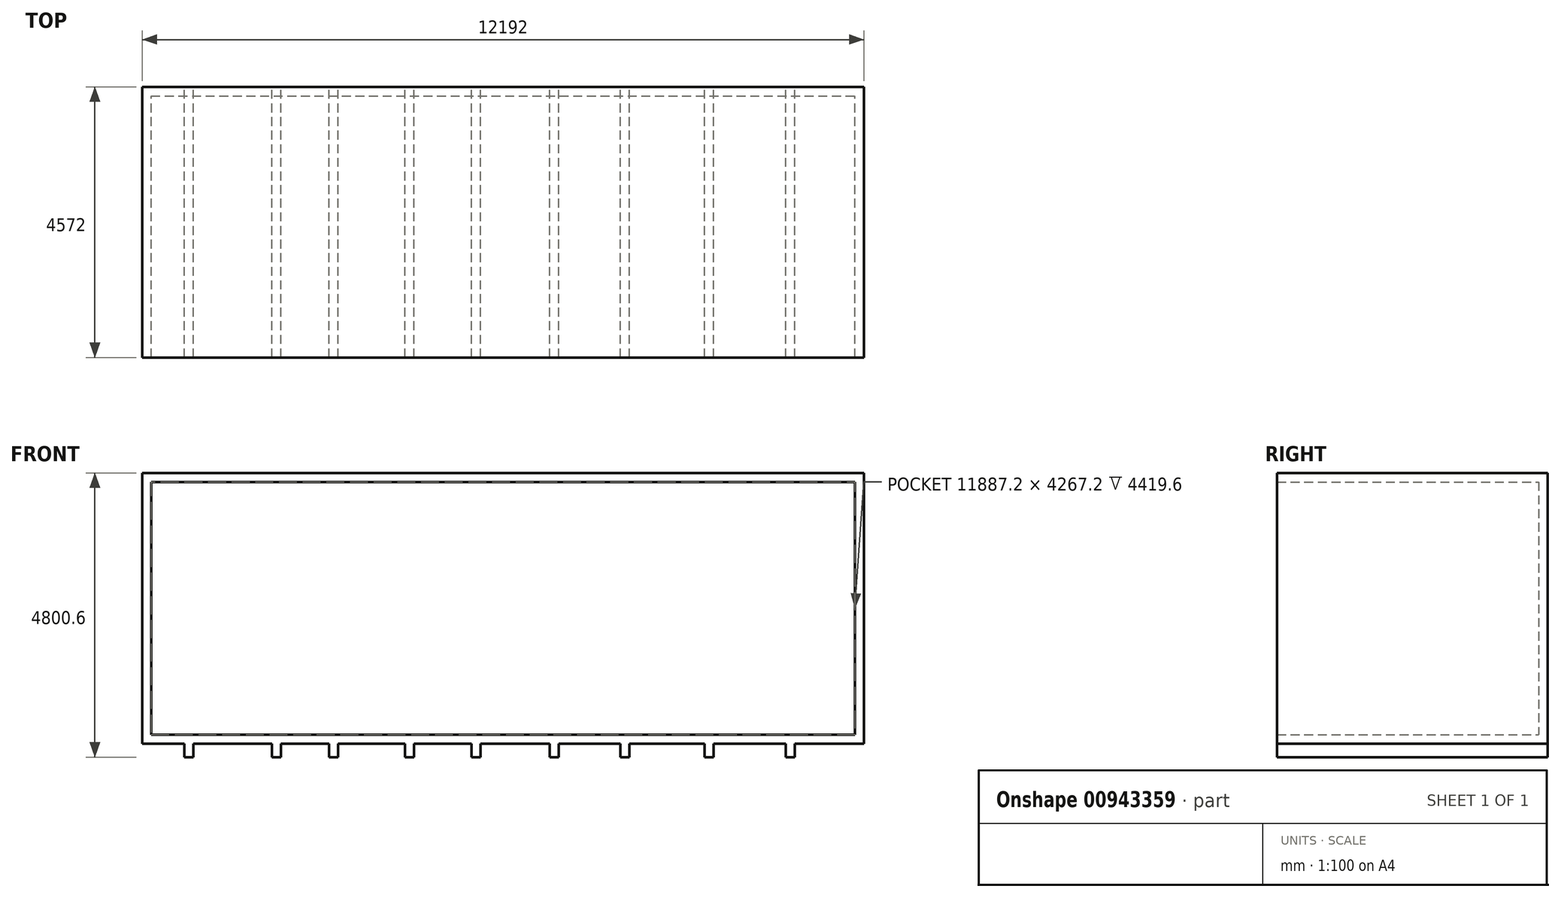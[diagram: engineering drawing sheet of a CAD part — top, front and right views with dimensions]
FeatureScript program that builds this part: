
annotation { "Feature Type Name" : "Feature", "Feature Type Description" : "" }
export const myFeature = defineFeature(function(context is Context, id is Id, definition is map)
    precondition{}
    {
        {
            var Q0;
            Q0=qCreatedBy(makeId("Front.planeOp"),FACE);
            var sketch = newSketch(context, id + "F0", { "sketchPlane" : qUnion([Q0])});
            skLineSegment(sketch, "E0.bottom", {"start": v(-6151.67, 2442.04) * mm, "end": v(6040.33, 2442.04) * mm});
            skLineSegment(sketch, "E0.top", {"start": v(-6151.67, -2129.96) * mm, "end": v(6040.33, -2129.96) * mm});
            skLineSegment(sketch, "E0.left", {"start": v(-6151.67, 2442.04) * mm, "end": v(-6151.67, -2129.96) * mm});
            skLineSegment(sketch, "E0.right", {"start": v(6040.33, 2442.04) * mm, "end": v(6040.33, -2129.96) * mm});
            skSolve(sketch);
        }
        {
            var Q0;
            Q0 = qSketchRegion(id + "F0", true);
            extrude(context, id + "F1", {"entities" : qUnion([Q0]), "depth" : 4572 * mm, "offsetDistance" : 25.4 * mm});
        }
        {
            var Q0;
            Q0=makeQuery(id+"F1.opExtrude","CAP_FACE",FACE,{"disambiguationData":[OSD([sQuery(id+"F0.wireOp",EDGE,"E0.bottom"),sQuery(id+"F0.wireOp",EDGE,"E0.top"),sQuery(id+"F0.wireOp",EDGE,"E0.left"),sQuery(id+"F0.wireOp",EDGE,"E0.right")])],"isStart":false});
            shell(context, id + "F2", {"entities" : qUnion([Q0]), "thickness" : 152.4 * mm});
        }
        {
            var Q0;
            Q0=makeQuery(id+"F1.opExtrude","SWEPT_FACE",FACE,{"disambiguationData":[OSD([sQuery(id+"F0.wireOp",EDGE,"E0.top")])]});
            var sketch = newSketch(context, id + "F3", { "sketchPlane" : qUnion([Q0])});
            skLineSegment(sketch, "E1.bottom", {"start": v(4875.4, 4572) * mm, "end": v(4723, 4572) * mm});
            skLineSegment(sketch, "E1.top", {"start": v(4875.4, 0) * mm, "end": v(4723, 0) * mm});
            skLineSegment(sketch, "E1.left", {"start": v(4875.4, 4572) * mm, "end": v(4875.4, 0) * mm});
            skLineSegment(sketch, "E1.right", {"start": v(4723, 4572) * mm, "end": v(4723, 0) * mm});
            skLineSegment(sketch, "E2.bottom", {"start": v(3502.69, 4572) * mm, "end": v(3350.29, 4572) * mm});
            skLineSegment(sketch, "E2.top", {"start": v(3502.69, 0) * mm, "end": v(3350.29, 0) * mm});
            skLineSegment(sketch, "E2.left", {"start": v(3502.69, 4572) * mm, "end": v(3502.69, 0) * mm});
            skLineSegment(sketch, "E2.right", {"start": v(3350.29, 4572) * mm, "end": v(3350.29, 0) * mm});
            skLineSegment(sketch, "E3.bottom", {"start": v(2076.49, 4572) * mm, "end": v(1924.09, 4572) * mm});
            skLineSegment(sketch, "E3.top", {"start": v(2076.49, 0) * mm, "end": v(1924.09, 0) * mm});
            skLineSegment(sketch, "E3.left", {"start": v(2076.49, 4572) * mm, "end": v(2076.49, 0) * mm});
            skLineSegment(sketch, "E3.right", {"start": v(1924.09, 4572) * mm, "end": v(1924.09, 0) * mm});
            skLineSegment(sketch, "E4.bottom", {"start": v(882.05, 4572) * mm, "end": v(729.65, 4572) * mm});
            skLineSegment(sketch, "E4.top", {"start": v(882.05, 0) * mm, "end": v(729.65, 0) * mm});
            skLineSegment(sketch, "E4.left", {"start": v(882.05, 4572) * mm, "end": v(882.05, 0) * mm});
            skLineSegment(sketch, "E4.right", {"start": v(729.65, 4572) * mm, "end": v(729.65, 0) * mm});
            skLineSegment(sketch, "E5.bottom", {"start": v(-437.18, 4572) * mm, "end": v(-589.58, 4572) * mm});
            skLineSegment(sketch, "E5.top", {"start": v(-437.18, 0) * mm, "end": v(-589.58, 0) * mm});
            skLineSegment(sketch, "E5.left", {"start": v(-437.18, 4572) * mm, "end": v(-437.18, 0) * mm});
            skLineSegment(sketch, "E5.right", {"start": v(-589.58, 4572) * mm, "end": v(-589.58, 0) * mm});
            skLineSegment(sketch, "E6.bottom", {"start": v(-1560.32, 4572) * mm, "end": v(-1712.72, 4572) * mm});
            skLineSegment(sketch, "E6.top", {"start": v(-1560.32, 0) * mm, "end": v(-1712.72, 0) * mm});
            skLineSegment(sketch, "E6.left", {"start": v(-1560.32, 4572) * mm, "end": v(-1560.32, 0) * mm});
            skLineSegment(sketch, "E6.right", {"start": v(-1712.72, 4572) * mm, "end": v(-1712.72, 0) * mm});
            skLineSegment(sketch, "E7.bottom", {"start": v(-2843.9, 4572) * mm, "end": v(-2996.3, 4572) * mm});
            skLineSegment(sketch, "E7.top", {"start": v(-2843.9, 0) * mm, "end": v(-2996.3, 0) * mm});
            skLineSegment(sketch, "E7.left", {"start": v(-2843.9, 4572) * mm, "end": v(-2843.9, 0) * mm});
            skLineSegment(sketch, "E7.right", {"start": v(-2996.3, 4572) * mm, "end": v(-2996.3, 0) * mm});
            skLineSegment(sketch, "E8.bottom", {"start": v(-3806.58, 4572) * mm, "end": v(-3958.98, 4572) * mm});
            skLineSegment(sketch, "E8.top", {"start": v(-3806.58, 0) * mm, "end": v(-3958.98, 0) * mm});
            skLineSegment(sketch, "E8.left", {"start": v(-3806.58, 4572) * mm, "end": v(-3806.58, 0) * mm});
            skLineSegment(sketch, "E8.right", {"start": v(-3958.98, 4572) * mm, "end": v(-3958.98, 0) * mm});
            skLineSegment(sketch, "E9.bottom", {"start": v(-5286.26, 4572) * mm, "end": v(-5438.66, 4572) * mm});
            skLineSegment(sketch, "E9.top", {"start": v(-5286.26, 0) * mm, "end": v(-5438.66, 0) * mm});
            skLineSegment(sketch, "E9.left", {"start": v(-5286.26, 4572) * mm, "end": v(-5286.26, 0) * mm});
            skLineSegment(sketch, "E9.right", {"start": v(-5438.66, 4572) * mm, "end": v(-5438.66, 0) * mm});
            skSolve(sketch);
        }
        {
            var Q0;
            Q0 = qSketchRegion(id + "F3", true);
            extrude(context, id + "F4", {"entities" : qUnion([Q0]), "operationType" : NewBodyOperationType.ADD, "depth" : 228.6 * mm, "offsetDistance" : 25.4 * mm});
        }
    });
